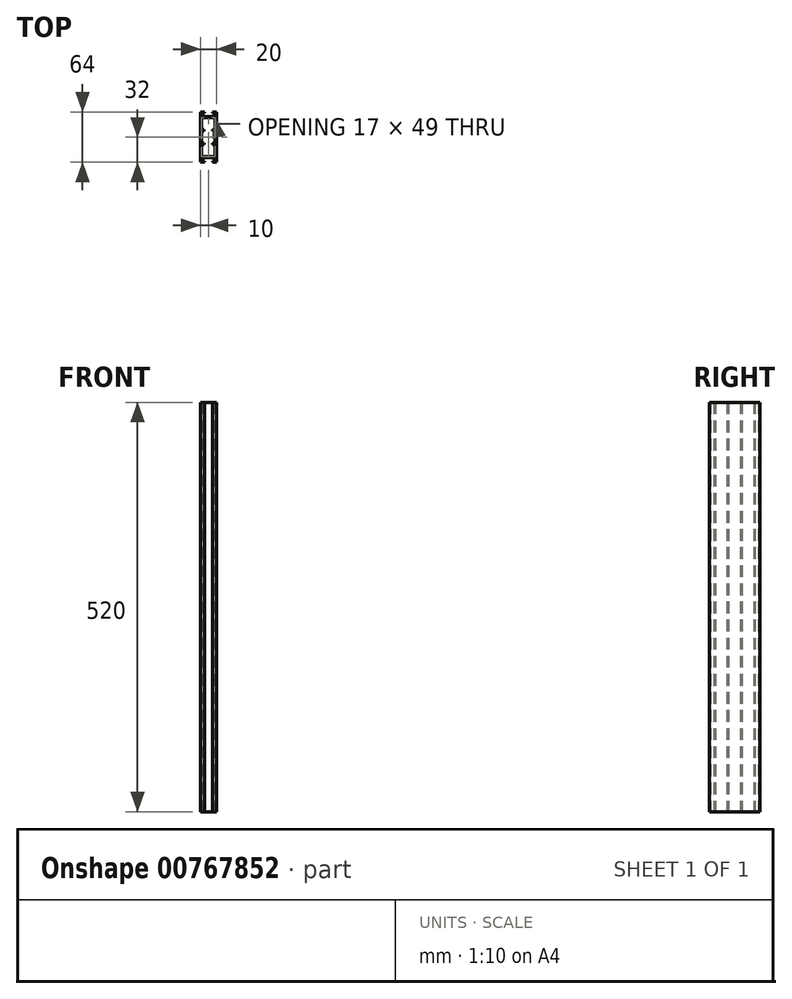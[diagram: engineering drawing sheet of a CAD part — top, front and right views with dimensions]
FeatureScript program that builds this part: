
annotation { "Feature Type Name" : "Feature", "Feature Type Description" : "" }
export const myFeature = defineFeature(function(context is Context, id is Id, definition is map)
    precondition{}
    {
        {
            var Q0;
            Q0=qCreatedBy(makeId("Top.planeOp"),FACE);
            var sketch = newSketch(context, id + "F0", { "sketchPlane" : qUnion([Q0])});
            skLineSegment(sketch, "E0", {"start": v(-5, 32) * mm, "end": v(-10, 32) * mm});
            skLineSegment(sketch, "E1", {"start": v(-10, 32) * mm, "end": v(-10, -32) * mm});
            skLineSegment(sketch, "E2", {"start": v(-10, -32) * mm, "end": v(-5, -32) * mm});
            skLineSegment(sketch, "E3", {"start": v(-5, -32) * mm, "end": v(-5, -30.5) * mm});
            skLineSegment(sketch, "E4", {"start": v(-5, -30.5) * mm, "end": v(-8.5, -30.5) * mm});
            skLineSegment(sketch, "E5", {"start": v(-8.5, -30.5) * mm, "end": v(-8.5, -26) * mm});
            skLineSegment(sketch, "E6", {"start": v(-8.5, -26) * mm, "end": v(8.5, -26) * mm});
            skLineSegment(sketch, "E7", {"start": v(8.5, -26) * mm, "end": v(8.5, -30.5) * mm});
            skLineSegment(sketch, "E8", {"start": v(8.5, -30.5) * mm, "end": v(5, -30.5) * mm});
            skLineSegment(sketch, "E9", {"start": v(5, -30.5) * mm, "end": v(5, -32) * mm});
            skLineSegment(sketch, "E10", {"start": v(5, -32) * mm, "end": v(10, -32) * mm});
            skLineSegment(sketch, "E11", {"start": v(10, -32) * mm, "end": v(10, 32) * mm});
            skLineSegment(sketch, "E12", {"start": v(10, 32) * mm, "end": v(5, 32) * mm});
            skLineSegment(sketch, "E13", {"start": v(5, 32) * mm, "end": v(5, 30.5) * mm});
            skLineSegment(sketch, "E14", {"start": v(5, 30.5) * mm, "end": v(8.5, 30.5) * mm});
            skLineSegment(sketch, "E15", {"start": v(8.5, 30.5) * mm, "end": v(8.5, 26) * mm});
            skLineSegment(sketch, "E16", {"start": v(8.5, 26) * mm, "end": v(-8.5, 26) * mm});
            skLineSegment(sketch, "E17", {"start": v(-8.5, 26) * mm, "end": v(-8.5, 30.5) * mm});
            skLineSegment(sketch, "E18", {"start": v(-8.5, 30.5) * mm, "end": v(-5, 30.5) * mm});
            skLineSegment(sketch, "E19", {"start": v(-5, 30.5) * mm, "end": v(-5, 32) * mm});
            skLineSegment(sketch, "E20", {"start": v(-8.5, 24.5) * mm, "end": v(-8.5, 9.5) * mm});
            skLineSegment(sketch, "E21", {"start": v(-8.5, 9.5) * mm, "end": v(-5.5, 9.5) * mm});
            skLineSegment(sketch, "E22", {"start": v(-5.5, 9.5) * mm, "end": v(-5.5, 7.5) * mm});
            skLineSegment(sketch, "E23", {"start": v(-5.5, 7.5) * mm, "end": v(-8.5, 7.5) * mm});
            skLineSegment(sketch, "E24", {"start": v(-8.5, 7.5) * mm, "end": v(-8.5, -7.5) * mm});
            skLineSegment(sketch, "E25", {"start": v(-8.5, -7.5) * mm, "end": v(-5.5, -7.5) * mm});
            skLineSegment(sketch, "E26", {"start": v(-5.5, -7.5) * mm, "end": v(-5.5, -9.5) * mm});
            skLineSegment(sketch, "E27", {"start": v(-5.5, -9.5) * mm, "end": v(-8.5, -9.5) * mm});
            skLineSegment(sketch, "E28", {"start": v(-8.5, -9.5) * mm, "end": v(-8.5, -24.5) * mm});
            skLineSegment(sketch, "E29", {"start": v(-8.5, -24.5) * mm, "end": v(8.5, -24.5) * mm});
            skLineSegment(sketch, "E30", {"start": v(8.5, -24.5) * mm, "end": v(8.5, -9.5) * mm});
            skLineSegment(sketch, "E31", {"start": v(8.5, -9.5) * mm, "end": v(5.5, -9.5) * mm});
            skLineSegment(sketch, "E32", {"start": v(5.5, -9.5) * mm, "end": v(5.5, -7.5) * mm});
            skLineSegment(sketch, "E33", {"start": v(5.5, -7.5) * mm, "end": v(8.5, -7.5) * mm});
            skLineSegment(sketch, "E34", {"start": v(8.5, -7.5) * mm, "end": v(8.5, 7.5) * mm});
            skLineSegment(sketch, "E35", {"start": v(8.5, 7.5) * mm, "end": v(5.5, 7.5) * mm});
            skLineSegment(sketch, "E36", {"start": v(5.5, 7.5) * mm, "end": v(5.5, 9.5) * mm});
            skLineSegment(sketch, "E37", {"start": v(5.5, 9.5) * mm, "end": v(8.5, 9.5) * mm});
            skLineSegment(sketch, "E38", {"start": v(8.5, 9.5) * mm, "end": v(8.5, 24.5) * mm});
            skLineSegment(sketch, "E39", {"start": v(8.5, 24.5) * mm, "end": v(-8.5, 24.5) * mm});
            skLineSegment(sketch, "E40", {"start": v(0, 26) * mm, "end": v(0, -26) * mm, "construction": true});
            skSolve(sketch);
        }
        {
            var Q0;
            Q0=makeQuery(id+"F0.imprint","IMPRINT",FACE,{"disambiguationData":[TD([[makeQuery(id+"F0.imprint","IMPRINT",EDGE,{"derivedFrom":sQuery(id+"F0.wireOp",EDGE,"E0")}),1.0]])]});
            extrude(context, id + "F1", {"entities" : qUnion([Q0]), "flatOperationType" : FlatOperationType.REMOVE, "depth" : 520 * mm, "offsetDistance" : 25 * mm, "domain" : OperationDomain.MODEL});
        }
    });
